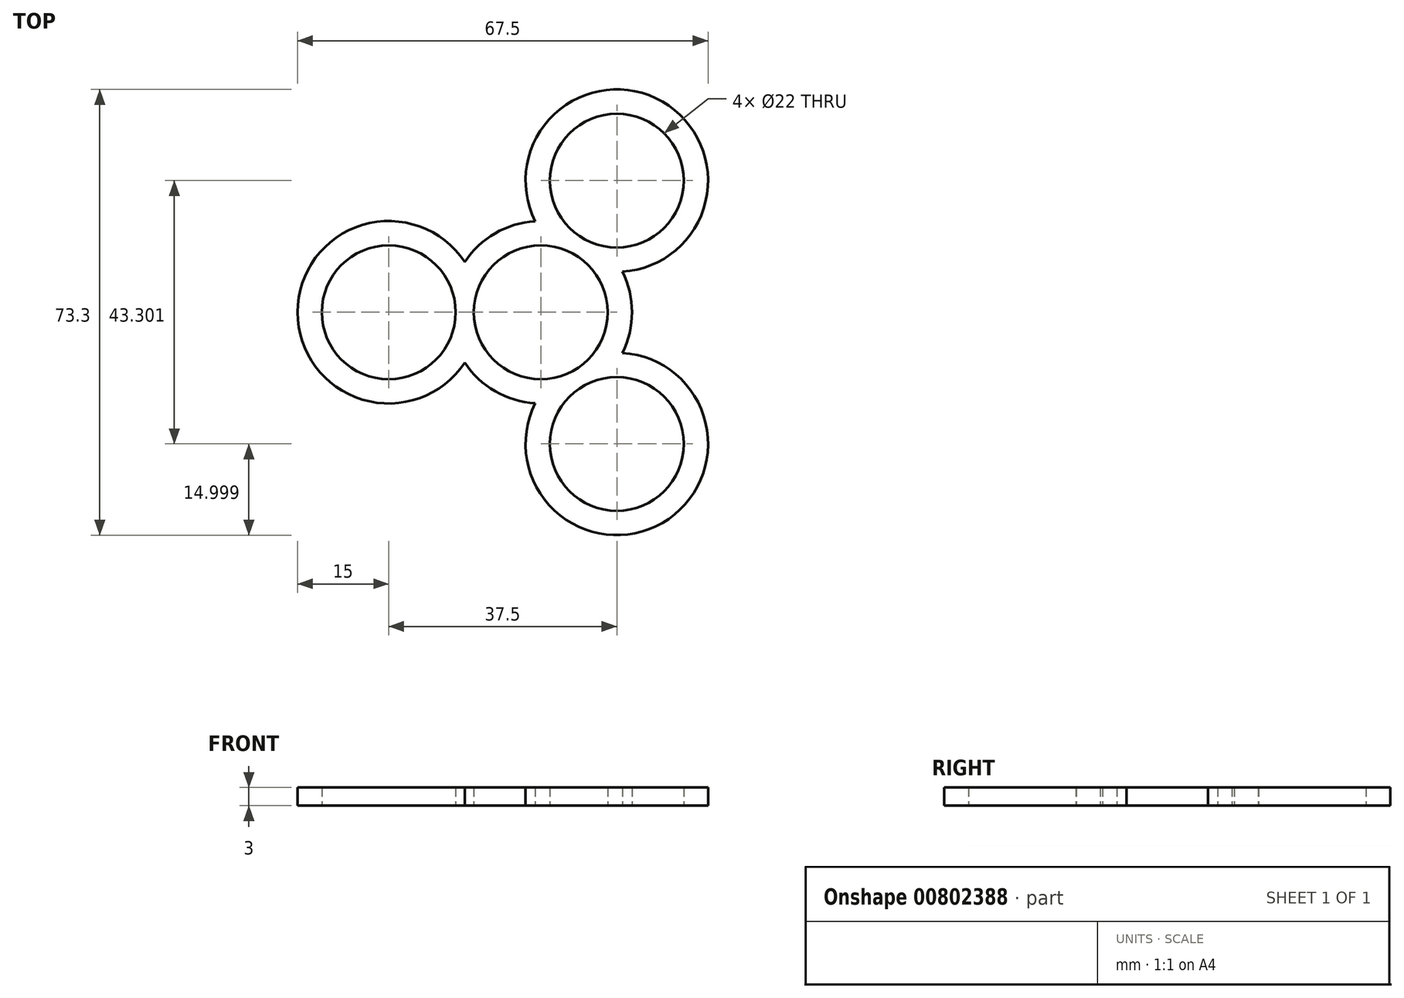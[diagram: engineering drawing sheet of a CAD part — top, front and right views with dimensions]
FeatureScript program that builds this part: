
annotation { "Feature Type Name" : "Feature", "Feature Type Description" : "" }
export const myFeature = defineFeature(function(context is Context, id is Id, definition is map)
    precondition{}
    {
        {
            var Q0;
            Q0=qCreatedBy(makeId("Top.planeOp"),FACE);
            var sketch = newSketch(context, id + "F0", { "sketchPlane" : qUnion([Q0])});
            skArc(sketch, "E0", {"start": v(-5.5, 9.53) * mm, "mid": v(-11, 0) * mm, "end": v(-5.5, -9.53) * mm});
            skCircle(sketch, "E1", {"center": v(-25, 0) * mm, "radius": 11 * mm});
            skArc(sketch, "E2", {"start": v(-12.5, 8.3) * mm, "mid": v(-40, 0) * mm, "end": v(-12.5, -8.3) * mm});
            skArc(sketch, "E3", {"start": v(-12.5, -8.3) * mm, "mid": v(-10.27, -10.93) * mm, "end": v(-7.5, -13) * mm});
            skArc(sketch, "E4.trimOffspring", {"start": v(-7.5, 13) * mm, "mid": v(-10.27, 10.93) * mm, "end": v(-12.5, 8.3) * mm});
            skArc(sketch, "E5.1.0", {"start": v(-0.93, -14.97) * mm, "mid": v(20, -34.64) * mm, "end": v(13.43, -6.68) * mm});
            skCircle(sketch, "E5.1.1", {"center": v(12.5, -21.65) * mm, "radius": 11 * mm});
            skArc(sketch, "E5.1.2", {"start": v(13.43, -6.68) * mm, "mid": v(14.6, -3.43) * mm, "end": v(15, 0) * mm});
            skArc(sketch, "E5.1.3", {"start": v(-5.5, -9.53) * mm, "mid": v(5.5, -9.53) * mm, "end": v(11, 0) * mm});
            skArc(sketch, "E5.1.4", {"start": v(-7.5, -13) * mm, "mid": v(-4.33, -14.36) * mm, "end": v(-0.93, -14.97) * mm});
            skArc(sketch, "E5.2.0", {"start": v(13.43, 6.68) * mm, "mid": v(20, 34.64) * mm, "end": v(-0.93, 14.97) * mm});
            skCircle(sketch, "E5.2.1", {"center": v(12.5, 21.65) * mm, "radius": 11 * mm});
            skArc(sketch, "E5.2.2", {"start": v(-0.93, 14.97) * mm, "mid": v(-4.33, 14.36) * mm, "end": v(-7.5, 13) * mm});
            skArc(sketch, "E5.2.3", {"start": v(11, 0) * mm, "mid": v(5.5, 9.53) * mm, "end": v(-5.5, 9.53) * mm});
            skArc(sketch, "E5.2.4", {"start": v(15, 0) * mm, "mid": v(14.6, 3.43) * mm, "end": v(13.43, 6.68) * mm});
            skSolve(sketch);
        }
        {
            var Q0;
            Q0 = qSketchRegion(id + "F0", true);
            extrude(context, id + "F1", {"entities" : qUnion([Q0]), "depth" : 3 * mm, "offsetDistance" : 25 * mm});
        }
    });
